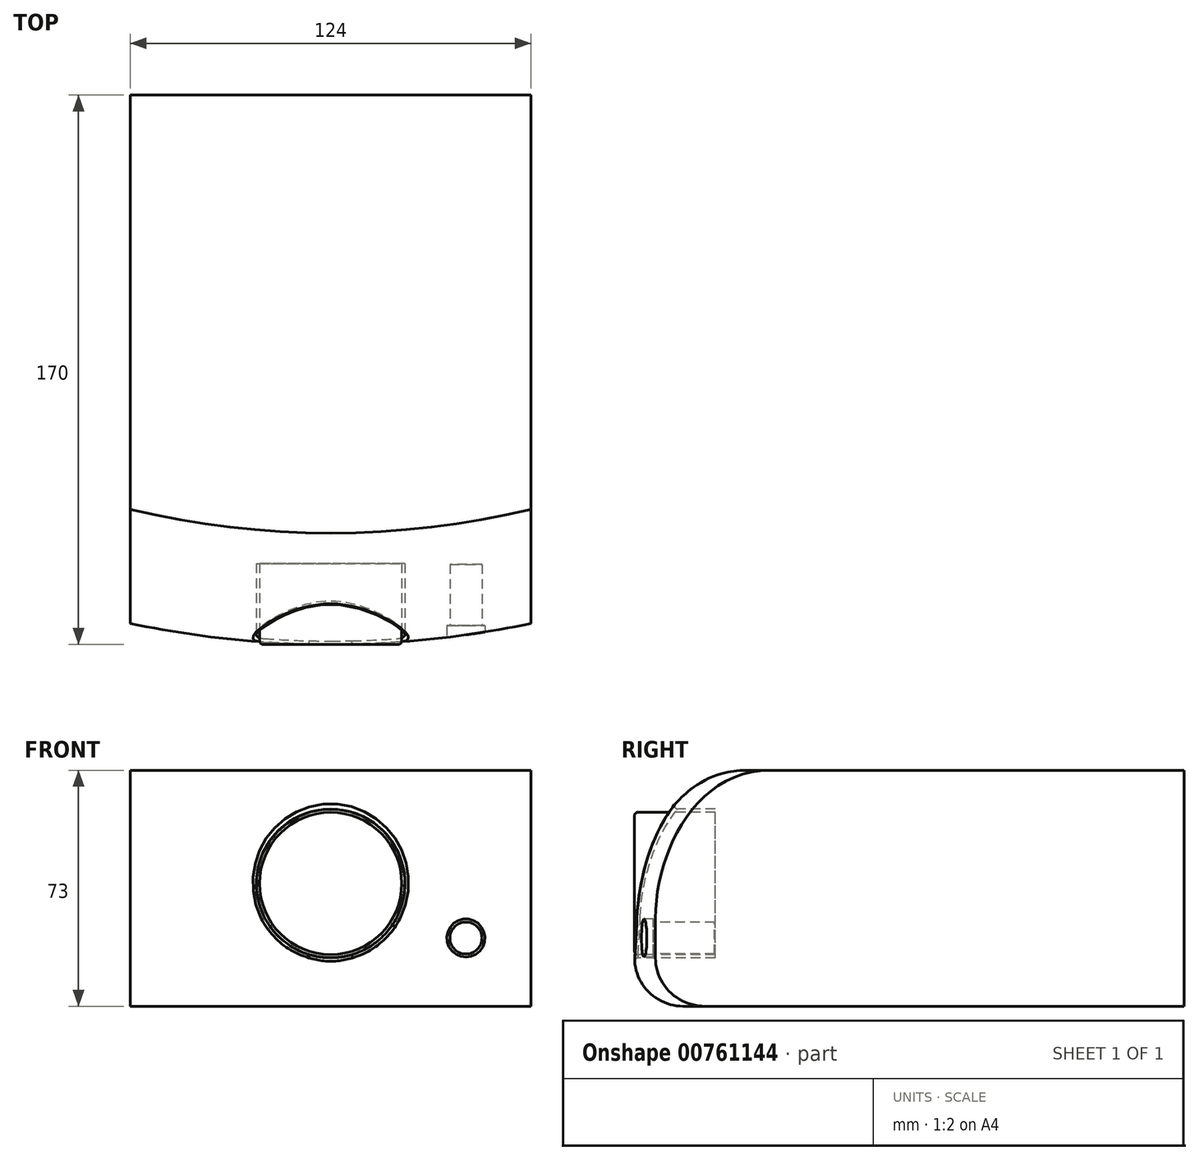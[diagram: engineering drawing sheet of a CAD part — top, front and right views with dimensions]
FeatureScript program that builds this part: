
annotation { "Feature Type Name" : "Feature", "Feature Type Description" : "" }
export const myFeature = defineFeature(function(context is Context, id is Id, definition is map)
    precondition{}
    {
        {
            var Q0;
            Q0=qCreatedBy(makeId("Top.planeOp"),FACE);
            var sketch = newSketch(context, id + "F0", { "sketchPlane" : qUnion([Q0])});
            skLineSegment(sketch, "E0.bottom", {"start": v(0, 170) * mm, "end": v(124, 170) * mm});
            skLineSegment(sketch, "E0.left", {"start": v(0, 170) * mm, "end": v(0, 6.48) * mm});
            skLineSegment(sketch, "E0.right", {"start": v(124, 170) * mm, "end": v(124, 6.48) * mm});
            skArc(sketch, "E1", {"start": v(0, 6.48) * mm, "mid": v(62, 0) * mm, "end": v(124, 6.48) * mm});
            skSolve(sketch);
        }
        {
            var Q0;
            Q0=makeQuery(id+"F0.imprint","IMPRINT",FACE,{"disambiguationData":[TD([[makeQuery(id+"F0.imprint","IMPRINT",EDGE,{"derivedFrom":sQuery(id+"F0.wireOp",EDGE,"E0.bottom")}),-1.0]])]});
            extrude(context, id + "F1", {"entities" : qUnion([Q0]), "depth" : 73 * mm, "offsetDistance" : 25 * mm});
        }
        {
            var Q0;
            Q0=makeQuery(id+"F1.opExtrude","SWEPT_FACE",FACE,{"disambiguationData":[OSD([sQuery(id+"F0.wireOp",EDGE,"E0.left")])]});
            var sketch = newSketch(context, id + "F2", { "sketchPlane" : qUnion([Q0])});
            skLineSegment(sketch, "E2.bottom", {"start": v(4.27, 73) * mm, "end": v(-41.77, 73) * mm});
            skLineSegment(sketch, "E2.top", {"start": v(4.27, 0) * mm, "end": v(-6.48, 0) * mm});
            skLineSegment(sketch, "E2.left", {"start": v(4.27, 73) * mm, "end": v(4.27, 0) * mm});
            skFitSpline(sketch, "E3", {"points": [v(-41.77, 73) * mm, v(-6.48, 27.19) * mm, v(-28.3, -2.16) * mm], "startDerivative": vector(122.64, 0) * mm, "endDerivative": vector(-94.15, 1.22) * mm});
            skLineSegment(sketch, "E4.right", {"start": v(-6.48, 0) * mm, "end": v(-6.48, 27.19) * mm});
            skSolve(sketch);
        }
        {
            var Q0;
            Q0 = qSketchRegion(id + "F2", true);
            var Q1;
            Q1=makeQuery(id+"F1.opExtrude","SWEPT_FACE",FACE,{"disambiguationData":[OSD([sQuery(id+"F0.wireOp",EDGE,"E1")])]});
            revolve(context, id + "F3", {"operationType" : NewBodyOperationType.REMOVE, "surfaceOperationType" : NewSurfaceOperationType.NEW, "entities" : qUnion([Q0]), "axis" : qUnion([Q1]), "revolveType" : RevolveType.FULL, "oppositeDirection" : true});
        }
        {
            var Q0;
            Q0=makeQuery(id+"F1.opExtrude","CAP_EDGE",EDGE,{"disambiguationData":[OSD([sQuery(id+"F0.wireOp",EDGE,"E1")])],"isStart":true});
            fillet(context, id + "F4", {"entities" : qUnion([Q0]), "radius" : 15 * mm, "tangentPropagation" : true, "allowEdgeOverflow" : false});
        }
        {
            var Q0;
            Q0=qCreatedBy(makeId("Front.planeOp"),FACE);
            var sketch = newSketch(context, id + "F5", { "sketchPlane" : qUnion([Q0])});
            skCircle(sketch, "E5", {"center": v(62, 38) * mm, "radius": 23 * mm});
            skSolve(sketch);
        }
        {
            var Q0;
            Q0 = qSketchRegion(id + "F5", true);
            extrude(context, id + "F6", {"entities" : qUnion([Q0]), "operationType" : NewBodyOperationType.REMOVE, "oppositeDirection" : true, "depth" : 25 * mm, "offsetDistance" : 25 * mm});
        }
        {
            var Q0;
            Q0=makeQuery(id+"F6.boolean.opBoolean","INTERSECT",EDGE,{"derivedFrom":[makeQuery(id+"F3.boolean.opBoolean","COPY",FACE,{"derivedFrom":makeQuery(id+"F3.opRevolve","SWEPT_FACE",FACE,{"disambiguationData":[OSD([sQuery(id+"F2.wireOp",EDGE,"E3")])]})}),makeQuery(id+"F6.opExtrude","SWEPT_FACE",FACE,{"disambiguationData":[OSD([sQuery(id+"F5.wireOp",EDGE,"E5")])]})]});
            fillet(context, id + "F7", {"entities" : qUnion([Q0]), "radius" : 1 * mm, "tangentPropagation" : true, "allowEdgeOverflow" : false});
        }
        {
            var Q0;
            Q0=qCreatedBy(makeId("Front.planeOp"),FACE);
            var sketch = newSketch(context, id + "F8", { "sketchPlane" : qUnion([Q0])});
            skCircle(sketch, "E6", {"center": v(62, 38) * mm, "radius": 22 * mm});
            skSolve(sketch);
        }
        {
            var Q0;
            Q0 = qSketchRegion(id + "F8", true);
            extrude(context, id + "F9", {"entities" : qUnion([Q0]), "oppositeDirection" : true, "depth" : 25 * mm, "offsetDistance" : 25 * mm});
        }
        {
            var Q0;
            Q0=makeQuery(id+"F9.opExtrude","CAP_EDGE",EDGE,{"disambiguationData":[OSD([sQuery(id+"F8.wireOp",EDGE,"E6")])],"isStart":true});
            fillet(context, id + "F10", {"entities" : qUnion([Q0]), "radius" : 1 * mm, "tangentPropagation" : true, "allowEdgeOverflow" : false});
        }
        {
            var Q0;
            Q0=qCreatedBy(makeId("Front.planeOp"),FACE);
            var sketch = newSketch(context, id + "F11", { "sketchPlane" : qUnion([Q0])});
            skCircle(sketch, "E7", {"center": v(103.85, 21.1) * mm, "radius": 5.9 * mm});
            skSolve(sketch);
        }
        {
            var Q0;
            Q0 = qSketchRegion(id + "F11", true);
            var Q1;
            {var subQ0=sQuery(id+"F0.wireOp",EDGE,"E1");var subQ1=makeQuery(id+"F1.opExtrude","SWEPT_FACE",FACE,{"disambiguationData":[OSD([subQ0])]});Q1=makeQuery(id+"F6.boolean.opBoolean","SPLIT",FACE,{"disambiguationData":[TD([makeQuery(id+"F1.opExtrude","SWEPT_FACE",FACE,{"disambiguationData":[OSD([sQuery(id+"F0.wireOp",EDGE,"E0.right")])]})])],"derivedFrom":subQ1});}
            extrude(context, id + "F12", {"entities" : qUnion([Q0]), "operationType" : NewBodyOperationType.REMOVE, "oppositeDirection" : true, "depth" : 5.78 * mm, "endBoundEntityFace" : qUnion([Q1]), "offsetDistance" : 25 * mm});
        }
        {
            var Q0;
            Q0=makeQuery(id+"F12.boolean.opBoolean","COPY",FACE,{"derivedFrom":makeQuery(id+"F12.opExtrude","CAP_FACE",FACE,{"disambiguationData":[OSD([sQuery(id+"F11.wireOp",EDGE,"E7")])],"isStart":false})});
            var sketch = newSketch(context, id + "F13", { "sketchPlane" : qUnion([Q0])});
            skCircle(sketch, "E8", {"center": v(103.85, 21.1) * mm, "radius": 4.95 * mm});
            skSolve(sketch);
        }
        {
            var Q0;
            Q0 = qSketchRegion(id + "F13", true);
            extrude(context, id + "F14", {"entities" : qUnion([Q0]), "operationType" : NewBodyOperationType.REMOVE, "oppositeDirection" : true, "depth" : 19 * mm, "offsetDistance" : 25 * mm});
        }
    });
